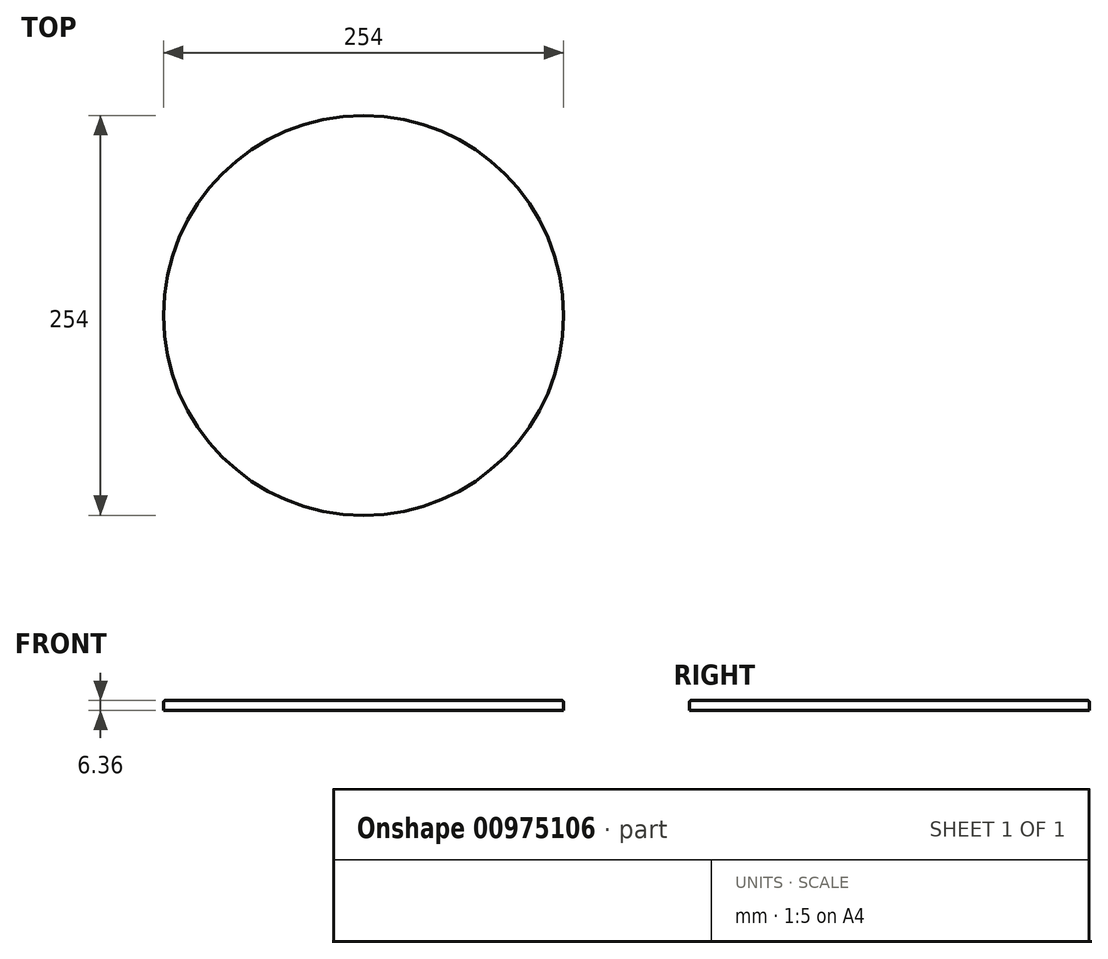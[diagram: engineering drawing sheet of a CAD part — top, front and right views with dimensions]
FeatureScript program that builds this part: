
annotation { "Feature Type Name" : "Feature", "Feature Type Description" : "" }
export const myFeature = defineFeature(function(context is Context, id is Id, definition is map)
    precondition{}
    {
        {
            var Q0;
            Q0=qCreatedBy(makeId("Top.planeOp"),FACE);
            var sketch = newSketch(context, id + "F0", { "sketchPlane" : qUnion([Q0])});
            skCircle(sketch, "E0", {"center": v(0, 0) * mm, "radius": 127 * mm});
            skSolve(sketch);
        }
        {
            var Q0;
            Q0=makeQuery(id+"F0.imprint","IMPRINT",FACE,{"disambiguationData":[TD([[makeQuery(id+"F0.imprint","IMPRINT",EDGE,{"derivedFrom":sQuery(id+"F0.wireOp",EDGE,"E0")}),1.0]])]});
            extrude(context, id + "F1", {"entities" : qUnion([Q0]), "endBound" : BoundingType.SYMMETRIC, "depth" : 6.35 * mm, "offsetDistance" : 25.4 * mm});
        }
        {
            var Q0;
            Q0=makeQuery(id+"F1.opExtrude","CAP_EDGE",EDGE,{"disambiguationData":[OSD([sQuery(id+"F0.wireOp",EDGE,"E0")])],"isStart":false});
            fillet(context, id + "F2", {"entities" : qUnion([Q0]), "radius" : 1.27 * mm, "tangentPropagation" : true, "allowEdgeOverflow" : false});
        }
    });
